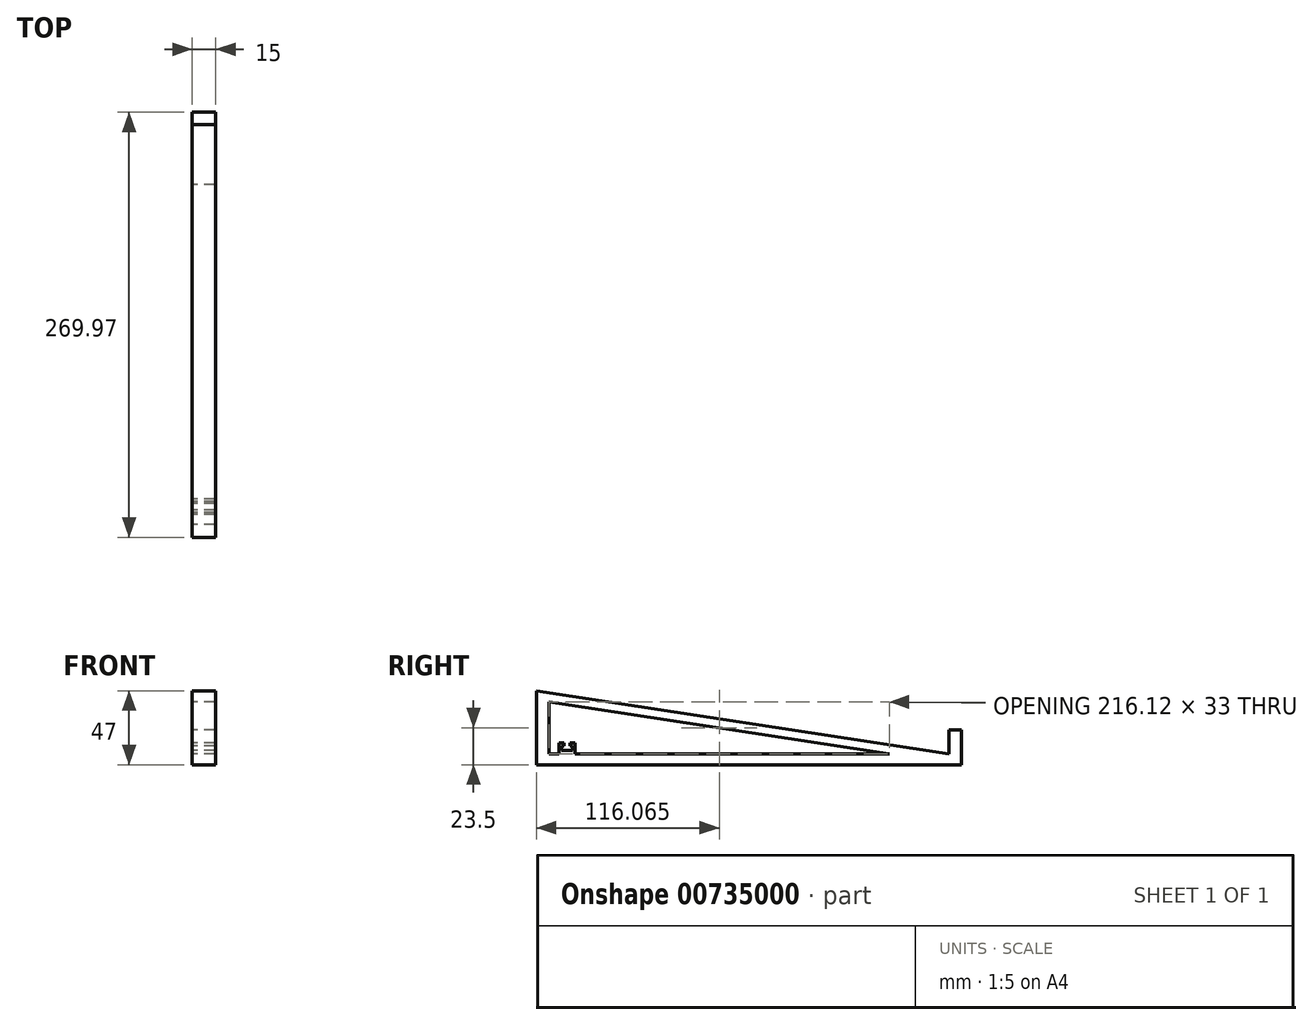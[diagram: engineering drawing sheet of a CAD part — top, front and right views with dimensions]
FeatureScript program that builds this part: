
annotation { "Feature Type Name" : "Feature", "Feature Type Description" : "" }
export const myFeature = defineFeature(function(context is Context, id is Id, definition is map)
    precondition{}
    {
        {
            var Q0;
            Q0=qCreatedBy(makeId("Right.planeOp"),FACE);
            var sketch = newSketch(context, id + "F0", { "sketchPlane" : qUnion([Q0])});
            skLineSegment(sketch, "E0", {"start": v(132.32, 0) * mm, "end": v(132.32, 22) * mm});
            skLineSegment(sketch, "E1", {"start": v(132.32, 22) * mm, "end": v(124.32, 22) * mm});
            skLineSegment(sketch, "E2", {"start": v(124.32, 22) * mm, "end": v(124.32, 7) * mm});
            skLineSegment(sketch, "E3", {"start": v(124.32, 7) * mm, "end": v(-137.65, 47) * mm});
            skLineSegment(sketch, "E4", {"start": v(-137.65, 47) * mm, "end": v(-137.65, 0) * mm});
            skLineSegment(sketch, "E5", {"start": v(-137.65, 0) * mm, "end": v(-129.65, 0) * mm});
            skLineSegment(sketch, "E6", {"start": v(-129.65, 0) * mm, "end": v(-129.65, 40) * mm});
            skLineSegment(sketch, "E7", {"start": v(-129.65, 40) * mm, "end": v(132.32, 0) * mm});
            skLineSegment(sketch, "E8", {"start": v(-129.65, 0) * mm, "end": v(132.32, 0) * mm});
            skLineSegment(sketch, "E9", {"start": v(-129.65, 7) * mm, "end": v(124.32, 7) * mm});
            skLineSegment(sketch, "E10", {"start": v(-123.3, 7) * mm, "end": v(-123.3, 14) * mm});
            skLineSegment(sketch, "E11", {"start": v(-123.3, 14) * mm, "end": v(-120.3, 14) * mm});
            skLineSegment(sketch, "E12", {"start": v(-120.3, 14) * mm, "end": v(-120.3, 12) * mm});
            skLineSegment(sketch, "E13", {"start": v(-120.3, 12) * mm, "end": v(-121.8, 12) * mm});
            skLineSegment(sketch, "E14", {"start": v(-121.8, 12) * mm, "end": v(-121.8, 9) * mm});
            skLineSegment(sketch, "E15", {"start": v(-121.8, 9) * mm, "end": v(-114.8, 9) * mm});
            skLineSegment(sketch, "E16", {"start": v(-114.8, 9) * mm, "end": v(-114.8, 12) * mm});
            skLineSegment(sketch, "E17", {"start": v(-114.8, 12) * mm, "end": v(-116.3, 12) * mm});
            skLineSegment(sketch, "E18", {"start": v(-116.3, 12) * mm, "end": v(-116.3, 14) * mm});
            skLineSegment(sketch, "E19", {"start": v(-116.3, 14) * mm, "end": v(-113.3, 14) * mm});
            skLineSegment(sketch, "E20", {"start": v(-113.3, 14) * mm, "end": v(-113.3, 7) * mm});
            skLineSegment(sketch, "E21", {"start": v(-113.3, 7) * mm, "end": v(-113.3, 14) * mm});
            skLineSegment(sketch, "E22", {"start": v(-113.3, 14) * mm, "end": v(-110.3, 14) * mm});
            skLineSegment(sketch, "E23", {"start": v(-110.3, 14) * mm, "end": v(-110.3, 12) * mm});
            skLineSegment(sketch, "E24", {"start": v(-110.3, 12) * mm, "end": v(-111.8, 12) * mm});
            skLineSegment(sketch, "E25", {"start": v(-111.8, 12) * mm, "end": v(-111.8, 9) * mm});
            skLineSegment(sketch, "E26", {"start": v(-111.8, 9) * mm, "end": v(-104.8, 9) * mm});
            skLineSegment(sketch, "E27", {"start": v(-104.8, 9) * mm, "end": v(-104.8, 12) * mm});
            skLineSegment(sketch, "E28", {"start": v(-104.8, 12) * mm, "end": v(-106.3, 12) * mm});
            skLineSegment(sketch, "E29", {"start": v(-106.3, 12) * mm, "end": v(-106.3, 14) * mm});
            skLineSegment(sketch, "E30", {"start": v(-106.3, 14) * mm, "end": v(-103.3, 14) * mm});
            skLineSegment(sketch, "E31", {"start": v(-103.3, 14) * mm, "end": v(-103.3, 7) * mm});
            skLineSegment(sketch, "E32", {"start": v(-103.3, 7) * mm, "end": v(-103.3, 14) * mm});
            skLineSegment(sketch, "E33", {"start": v(-103.3, 14) * mm, "end": v(-100.3, 14) * mm});
            skLineSegment(sketch, "E34", {"start": v(-100.3, 14) * mm, "end": v(-100.3, 12) * mm});
            skLineSegment(sketch, "E35", {"start": v(-100.3, 12) * mm, "end": v(-101.8, 12) * mm});
            skLineSegment(sketch, "E36", {"start": v(-101.8, 12) * mm, "end": v(-101.8, 9) * mm});
            skLineSegment(sketch, "E37", {"start": v(-101.8, 9) * mm, "end": v(-94.8, 9) * mm});
            skLineSegment(sketch, "E38", {"start": v(-94.8, 9) * mm, "end": v(-94.8, 12) * mm});
            skLineSegment(sketch, "E39", {"start": v(-94.8, 12) * mm, "end": v(-96.3, 12) * mm});
            skLineSegment(sketch, "E40", {"start": v(-96.3, 12) * mm, "end": v(-96.3, 14) * mm});
            skLineSegment(sketch, "E41", {"start": v(-96.3, 14) * mm, "end": v(-93.3, 14) * mm});
            skLineSegment(sketch, "E42", {"start": v(-93.3, 14) * mm, "end": v(-93.3, 7) * mm});
            skSolve(sketch);
        }
        {
            var Q0;
            Q0=qSketchRegion(id+"F0",true);
            var Q1;
            {var subQ0=sQuery(id+"F0.wireOp",EDGE,"E10");Q1=makeQuery(id+"F0.imprint","IMPRINT",FACE,{"disambiguationData":[TD([[makeQuery(id+"F0.imprint","IMPRINT",EDGE,{"derivedFrom":subQ0}),-1.0]])]});}
            var Q2;
            {var subQ0=sQuery(id+"F0.wireOp",EDGE,"E21");Q2=makeQuery(id+"F0.imprint","IMPRINT",FACE,{"disambiguationData":[TD([[makeQuery(id+"F0.imprint","IMPRINT",EDGE,{"derivedFrom":subQ0}),-1.0]])]});}
            var Q3;
            {var subQ0=sQuery(id+"F0.wireOp",EDGE,"E32");Q3=makeQuery(id+"F0.imprint","IMPRINT",FACE,{"disambiguationData":[TD([[makeQuery(id+"F0.imprint","IMPRINT",EDGE,{"derivedFrom":subQ0}),-1.0]])]});}
            extrude(context, id + "F1", {"entities" : qUnion([Q0, Q1, Q2, Q3]), "depth" : 15 * mm, "offsetDistance" : 25 * mm});
        }
    });
